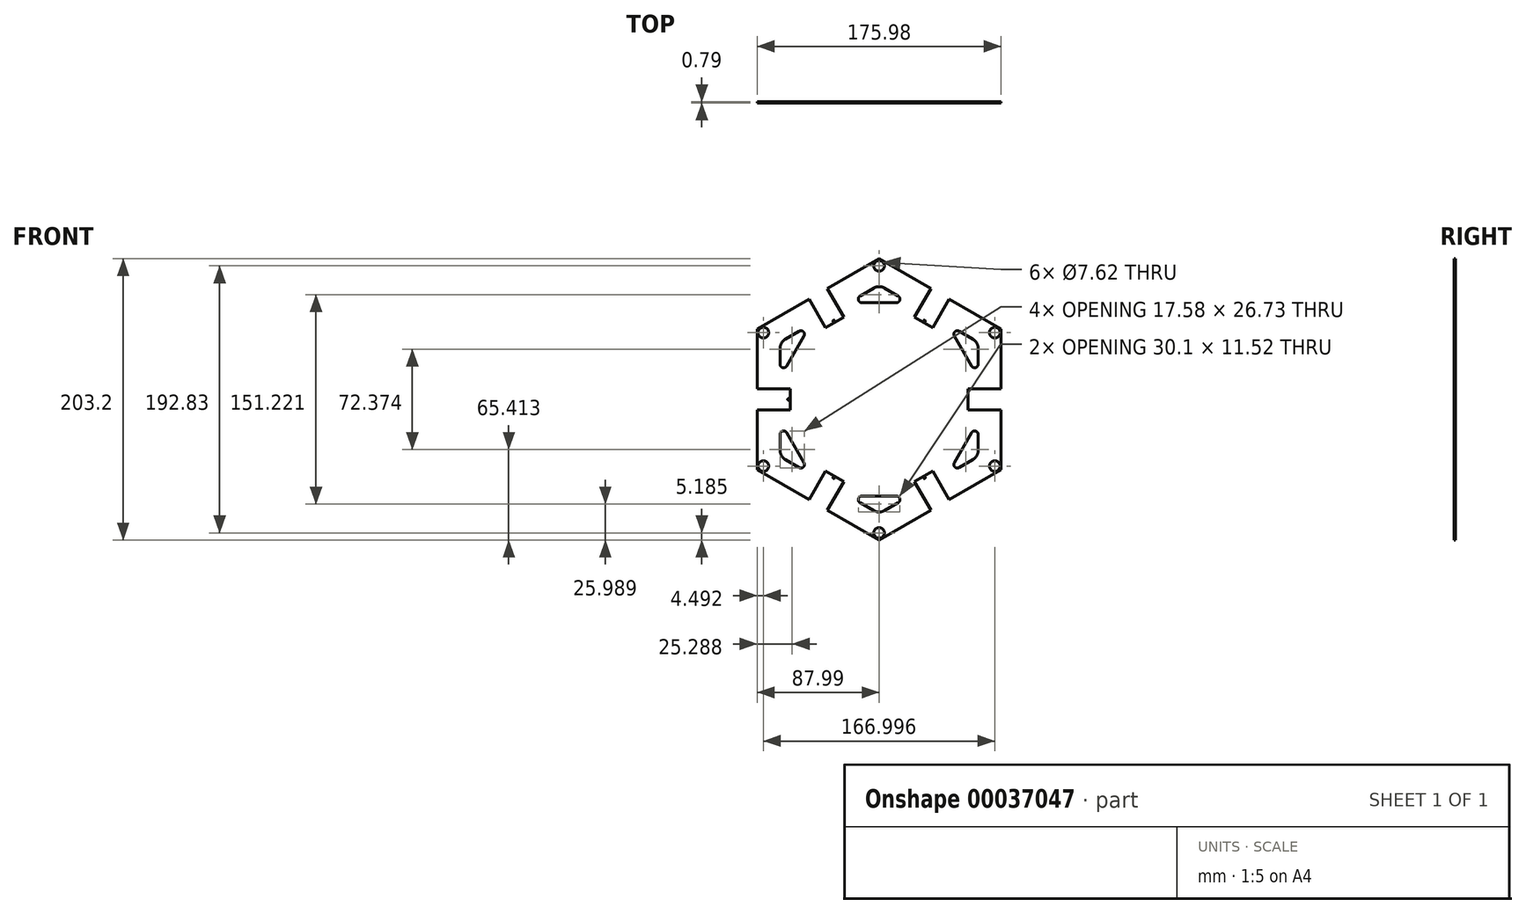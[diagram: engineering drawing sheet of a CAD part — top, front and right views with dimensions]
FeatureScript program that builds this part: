
annotation { "Feature Type Name" : "Feature", "Feature Type Description" : "" }
export const myFeature = defineFeature(function(context is Context, id is Id, definition is map)
    precondition{}
    {
        {
            var Q0;
            Q0=qCreatedBy(makeId("Front.planeOp"),FACE);
            var sketch = newSketch(context, id + "F0", { "sketchPlane" : qUnion([Q0])});
            skCircle(sketch, "E0.cCircle", {"center": v(0, 0) * mm, "radius": 87.99 * mm, "construction": true});
            skLineSegment(sketch, "E0.0", {"start": v(0, 101.6) * mm, "end": v(87.99, 50.8) * mm});
            skLineSegment(sketch, "E0.1", {"start": v(87.99, 50.8) * mm, "end": v(87.99, -50.8) * mm});
            skLineSegment(sketch, "E0.2", {"start": v(87.99, -50.8) * mm, "end": v(0, -101.6) * mm});
            skLineSegment(sketch, "E0.3", {"start": v(0, -101.6) * mm, "end": v(-87.99, -50.8) * mm});
            skLineSegment(sketch, "E0.4", {"start": v(-87.99, -50.8) * mm, "end": v(-87.99, 50.8) * mm});
            skLineSegment(sketch, "E0.5", {"start": v(-87.99, 50.8) * mm, "end": v(0, 101.6) * mm});
            skPoint(sketch, "E0.0.midPoint", {"position": v(44, 76.2) * mm});
            skSolve(sketch);
        }
        {
            var Q0;
            Q0=qSketchRegion(id+"F0",true);
            extrude(context, id + "F1", {"entities" : qUnion([Q0]), "depth" : 0.8 * mm});
        }
        {
            var Q0;
            Q0=makeQuery(id+"F1.opExtrude","CAP_FACE",FACE,{"disambiguationData":[OSD([sQuery(id+"F0.wireOp",EDGE,"E0.0"),sQuery(id+"F0.wireOp",EDGE,"E0.1"),sQuery(id+"F0.wireOp",EDGE,"E0.2"),sQuery(id+"F0.wireOp",EDGE,"E0.3"),sQuery(id+"F0.wireOp",EDGE,"E0.4"),sQuery(id+"F0.wireOp",EDGE,"E0.5")])],"isStart":false});
            var sketch = newSketch(context, id + "F2", { "sketchPlane" : qUnion([Q0])});
            skSolve(sketch);
        }
        {
            var Q0;
            Q0=qCreatedBy(makeId("Front.planeOp"),FACE);
            var sketch = newSketch(context, id + "F3", { "sketchPlane" : qUnion([Q0])});
            skLineSegment(sketch, "E1.bottom", {"start": v(87.99, 10.16) * mm, "end": v(102.7, 10.16) * mm});
            skLineSegment(sketch, "E1.top", {"start": v(87.99, -10.16) * mm, "end": v(102.7, -10.16) * mm});
            skLineSegment(sketch, "E1.left", {"start": v(87.99, 10.16) * mm, "end": v(87.99, -10.16) * mm});
            skLineSegment(sketch, "E1.right", {"start": v(102.7, 10.16) * mm, "end": v(102.7, -10.16) * mm});
            skPoint(sketch, "E2", {"position": v(87.99, 0) * mm});
            skLineSegment(sketch, "E3.1.0", {"start": v(52.8, -71.12) * mm, "end": v(60.15, -83.86) * mm});
            skLineSegment(sketch, "E3.1.1", {"start": v(52.8, -71.12) * mm, "end": v(35.2, -81.28) * mm});
            skLineSegment(sketch, "E3.1.2", {"start": v(60.15, -83.86) * mm, "end": v(42.55, -94.02) * mm});
            skLineSegment(sketch, "E3.1.3", {"start": v(35.2, -81.28) * mm, "end": v(42.55, -94.02) * mm});
            skLineSegment(sketch, "E3.2.0", {"start": v(-35.2, -81.28) * mm, "end": v(-42.55, -94.02) * mm});
            skLineSegment(sketch, "E3.2.1", {"start": v(-35.2, -81.28) * mm, "end": v(-52.8, -71.12) * mm});
            skLineSegment(sketch, "E3.2.2", {"start": v(-42.55, -94.02) * mm, "end": v(-60.15, -83.86) * mm});
            skLineSegment(sketch, "E3.2.3", {"start": v(-52.8, -71.12) * mm, "end": v(-60.15, -83.86) * mm});
            skLineSegment(sketch, "E3.3.0", {"start": v(-87.99, -10.16) * mm, "end": v(-102.7, -10.16) * mm});
            skLineSegment(sketch, "E3.3.1", {"start": v(-87.99, -10.16) * mm, "end": v(-87.99, 10.16) * mm});
            skLineSegment(sketch, "E3.3.2", {"start": v(-102.7, -10.16) * mm, "end": v(-102.7, 10.16) * mm});
            skLineSegment(sketch, "E3.3.3", {"start": v(-87.99, 10.16) * mm, "end": v(-102.7, 10.16) * mm});
            skLineSegment(sketch, "E3.4.0", {"start": v(-52.8, 71.12) * mm, "end": v(-60.15, 83.86) * mm});
            skLineSegment(sketch, "E3.4.1", {"start": v(-52.8, 71.12) * mm, "end": v(-35.2, 81.28) * mm});
            skLineSegment(sketch, "E3.4.2", {"start": v(-60.15, 83.86) * mm, "end": v(-42.55, 94.02) * mm});
            skLineSegment(sketch, "E3.4.3", {"start": v(-35.2, 81.28) * mm, "end": v(-42.55, 94.02) * mm});
            skLineSegment(sketch, "E3.5.0", {"start": v(35.2, 81.28) * mm, "end": v(42.55, 94.02) * mm});
            skLineSegment(sketch, "E3.5.1", {"start": v(35.2, 81.28) * mm, "end": v(52.8, 71.12) * mm});
            skLineSegment(sketch, "E3.5.2", {"start": v(42.55, 94.02) * mm, "end": v(60.15, 83.86) * mm});
            skLineSegment(sketch, "E3.5.3", {"start": v(52.8, 71.12) * mm, "end": v(60.15, 83.86) * mm});
            skPoint(sketch, "E3.center", {"position": v(0, 0) * mm});
            skLineSegment(sketch, "E3.anchor1", {"start": v(0, 0) * mm, "end": v(87.99, 10.16) * mm, "construction": true});
            skLineSegment(sketch, "E3.anchor2", {"start": v(0, 0) * mm, "end": v(35.2, 81.28) * mm, "construction": true});
            skPoint(sketch, "E4.1.0", {"position": v(48.34, 83.72) * mm});
            skPoint(sketch, "E4.2.0", {"position": v(-48.34, 83.72) * mm});
            skPoint(sketch, "E4.3.0", {"position": v(-96.67, 0) * mm});
            skPoint(sketch, "E4.4.0", {"position": v(-48.34, -83.72) * mm});
            skPoint(sketch, "E4.5.0", {"position": v(48.34, -83.72) * mm});
            skSolve(sketch);
        }
        {
            var Q0;
            Q0=makeQuery(id+"F2.imprint","IMPRINT",FACE,{"disambiguationData":[TD([[makeQuery(id+"F2.imprint","IMPRINT",EDGE,{"derivedFrom":makeQuery(id+"F1.opExtrude","CAP_EDGE",EDGE,{"disambiguationData":[OSD([sQuery(id+"F0.wireOp",EDGE,"E0.0")])],"isStart":false})}),-1.0]])]});
            var sketch = newSketch(context, id + "F4", { "sketchPlane" : qUnion([Q0])});
            skPoint(sketch, "E5.0", {"position": v(93.15, 0) * mm});
            skLineSegment(sketch, "E6.bottom", {"start": v(64, 7.62) * mm, "end": v(94.49, 7.62) * mm});
            skLineSegment(sketch, "E6.top", {"start": v(64, -7.62) * mm, "end": v(94.49, -7.62) * mm});
            skLineSegment(sketch, "E6.left", {"start": v(64, 7.62) * mm, "end": v(64, -7.62) * mm});
            skLineSegment(sketch, "E6.right", {"start": v(94.49, 7.62) * mm, "end": v(94.49, -7.62) * mm});
            skPoint(sketch, "E7", {"position": v(64, 0) * mm});
            skLineSegment(sketch, "E8", {"start": v(64, 0) * mm, "end": v(65.35, 0) * mm, "construction": true});
            skLineSegment(sketch, "E9", {"start": v(93.15, 0) * mm, "end": v(94.49, 0) * mm, "construction": true});
            skPoint(sketch, "E10.1.0", {"position": v(32.67, 56.6) * mm});
            skPoint(sketch, "E10.1.1", {"position": v(32, 55.43) * mm});
            skLineSegment(sketch, "E10.1.2", {"start": v(38.6, 51.62) * mm, "end": v(53.84, 78.02) * mm});
            skLineSegment(sketch, "E10.1.3", {"start": v(25.4, 59.24) * mm, "end": v(40.64, 85.64) * mm});
            skPoint(sketch, "E10.1.4", {"position": v(46.57, 80.67) * mm});
            skLineSegment(sketch, "E10.1.5", {"start": v(40.64, 85.64) * mm, "end": v(53.84, 78.02) * mm});
            skLineSegment(sketch, "E10.1.6", {"start": v(32, 55.43) * mm, "end": v(32.67, 56.6) * mm, "construction": true});
            skLineSegment(sketch, "E10.1.7", {"start": v(25.4, 59.24) * mm, "end": v(38.6, 51.62) * mm});
            skCircle(sketch, "E10.1.8", {"center": v(46.57, 80.67) * mm, "radius": 0.64 * mm});
            skCircle(sketch, "E10.1.9", {"center": v(32.67, 56.6) * mm, "radius": 0.64 * mm});
            skLineSegment(sketch, "E10.1.10", {"start": v(46.57, 80.67) * mm, "end": v(47.24, 81.83) * mm, "construction": true});
            skPoint(sketch, "E10.2.0", {"position": v(-32.67, 56.6) * mm});
            skPoint(sketch, "E10.2.1", {"position": v(-32, 55.43) * mm});
            skLineSegment(sketch, "E10.2.2", {"start": v(-25.4, 59.24) * mm, "end": v(-40.64, 85.64) * mm});
            skLineSegment(sketch, "E10.2.3", {"start": v(-38.6, 51.62) * mm, "end": v(-53.84, 78.02) * mm});
            skPoint(sketch, "E10.2.4", {"position": v(-46.57, 80.67) * mm});
            skLineSegment(sketch, "E10.2.5", {"start": v(-53.84, 78.02) * mm, "end": v(-40.64, 85.64) * mm});
            skLineSegment(sketch, "E10.2.6", {"start": v(-32, 55.43) * mm, "end": v(-32.67, 56.6) * mm, "construction": true});
            skLineSegment(sketch, "E10.2.7", {"start": v(-38.6, 51.62) * mm, "end": v(-25.4, 59.24) * mm});
            skCircle(sketch, "E10.2.8", {"center": v(-46.57, 80.67) * mm, "radius": 0.64 * mm});
            skCircle(sketch, "E10.2.9", {"center": v(-32.67, 56.6) * mm, "radius": 0.64 * mm});
            skLineSegment(sketch, "E10.2.10", {"start": v(-46.57, 80.67) * mm, "end": v(-47.24, 81.83) * mm, "construction": true});
            skPoint(sketch, "E10.3.0", {"position": v(-65.35, 0) * mm});
            skPoint(sketch, "E10.3.1", {"position": v(-64, 0) * mm});
            skLineSegment(sketch, "E10.3.2", {"start": v(-64, 7.62) * mm, "end": v(-94.49, 7.62) * mm});
            skLineSegment(sketch, "E10.3.3", {"start": v(-64, -7.62) * mm, "end": v(-94.49, -7.62) * mm});
            skPoint(sketch, "E10.3.4", {"position": v(-93.15, 0) * mm});
            skLineSegment(sketch, "E10.3.5", {"start": v(-94.49, -7.62) * mm, "end": v(-94.49, 7.62) * mm});
            skLineSegment(sketch, "E10.3.6", {"start": v(-64, 0) * mm, "end": v(-65.35, 0) * mm, "construction": true});
            skLineSegment(sketch, "E10.3.7", {"start": v(-64, -7.62) * mm, "end": v(-64, 7.62) * mm});
            skCircle(sketch, "E10.3.8", {"center": v(-93.15, 0) * mm, "radius": 0.64 * mm});
            skCircle(sketch, "E10.3.9", {"center": v(-65.35, 0) * mm, "radius": 0.64 * mm});
            skLineSegment(sketch, "E10.3.10", {"start": v(-93.15, 0) * mm, "end": v(-94.49, 0) * mm, "construction": true});
            skPoint(sketch, "E10.4.0", {"position": v(-32.67, -56.6) * mm});
            skPoint(sketch, "E10.4.1", {"position": v(-32, -55.43) * mm});
            skLineSegment(sketch, "E10.4.2", {"start": v(-38.6, -51.62) * mm, "end": v(-53.84, -78.02) * mm});
            skLineSegment(sketch, "E10.4.3", {"start": v(-25.4, -59.24) * mm, "end": v(-40.64, -85.64) * mm});
            skPoint(sketch, "E10.4.4", {"position": v(-46.57, -80.67) * mm});
            skLineSegment(sketch, "E10.4.5", {"start": v(-40.64, -85.64) * mm, "end": v(-53.84, -78.02) * mm});
            skLineSegment(sketch, "E10.4.6", {"start": v(-32, -55.43) * mm, "end": v(-32.67, -56.6) * mm, "construction": true});
            skLineSegment(sketch, "E10.4.7", {"start": v(-25.4, -59.24) * mm, "end": v(-38.6, -51.62) * mm});
            skCircle(sketch, "E10.4.8", {"center": v(-46.57, -80.67) * mm, "radius": 0.64 * mm});
            skCircle(sketch, "E10.4.9", {"center": v(-32.67, -56.6) * mm, "radius": 0.64 * mm});
            skLineSegment(sketch, "E10.4.10", {"start": v(-46.57, -80.67) * mm, "end": v(-47.24, -81.83) * mm, "construction": true});
            skPoint(sketch, "E10.5.0", {"position": v(32.67, -56.6) * mm});
            skPoint(sketch, "E10.5.1", {"position": v(32, -55.43) * mm});
            skLineSegment(sketch, "E10.5.2", {"start": v(25.4, -59.24) * mm, "end": v(40.64, -85.64) * mm});
            skLineSegment(sketch, "E10.5.3", {"start": v(38.6, -51.62) * mm, "end": v(53.84, -78.02) * mm});
            skPoint(sketch, "E10.5.4", {"position": v(46.57, -80.67) * mm});
            skLineSegment(sketch, "E10.5.5", {"start": v(53.84, -78.02) * mm, "end": v(40.64, -85.64) * mm});
            skLineSegment(sketch, "E10.5.6", {"start": v(32, -55.43) * mm, "end": v(32.67, -56.6) * mm, "construction": true});
            skLineSegment(sketch, "E10.5.7", {"start": v(38.6, -51.62) * mm, "end": v(25.4, -59.24) * mm});
            skCircle(sketch, "E10.5.8", {"center": v(46.57, -80.67) * mm, "radius": 0.64 * mm});
            skCircle(sketch, "E10.5.9", {"center": v(32.67, -56.6) * mm, "radius": 0.64 * mm});
            skLineSegment(sketch, "E10.5.10", {"start": v(46.57, -80.67) * mm, "end": v(47.24, -81.83) * mm, "construction": true});
            skPoint(sketch, "E10.center", {"position": v(0, 0) * mm});
            skSolve(sketch);
        }
        {
            var Q0;
            Q0=qSketchRegion(id+"F4",true);
            extrude(context, id + "F5", {"entities" : qUnion([Q0]), "operationType" : NewBodyOperationType.REMOVE, "endBound" : BoundingType.THROUGH_ALL, "oppositeDirection" : true, "depth" : 25.4 * mm});
        }
        {
            var Q0;
            Q0=makeQuery(id+"F2.imprint","IMPRINT",FACE,{"disambiguationData":[TD([[makeQuery(id+"F2.imprint","IMPRINT",EDGE,{"derivedFrom":makeQuery(id+"F1.opExtrude","CAP_EDGE",EDGE,{"disambiguationData":[OSD([sQuery(id+"F0.wireOp",EDGE,"E0.0")])],"isStart":false})}),-1.0]])]});
            var sketch = newSketch(context, id + "F6", { "sketchPlane" : qUnion([Q0])});
            skLineSegment(sketch, "E11", {"start": v(91.28, 52.7) * mm, "end": v(75.72, 43.72) * mm, "construction": true});
            skLineSegment(sketch, "E12", {"start": v(75.72, 43.72) * mm, "end": v(79, 55.98) * mm, "construction": true});
            skLineSegment(sketch, "E13", {"start": v(79, 55.98) * mm, "end": v(91.28, 52.7) * mm, "construction": true});
            skLineSegment(sketch, "E14", {"start": v(91.28, 52.7) * mm, "end": v(87.99, 40.43) * mm, "construction": true});
            skLineSegment(sketch, "E15", {"start": v(87.99, 40.43) * mm, "end": v(75.72, 43.72) * mm, "construction": true});
            skPoint(sketch, "E16", {"position": v(83.5, 48.2) * mm});
            skPoint(sketch, "E17.1.0", {"position": v(0, 96.42) * mm});
            skPoint(sketch, "E17.2.0", {"position": v(-83.5, 48.2) * mm});
            skPoint(sketch, "E17.3.0", {"position": v(-83.5, -48.2) * mm});
            skPoint(sketch, "E17.4.0", {"position": v(0, -96.42) * mm});
            skPoint(sketch, "E17.5.0", {"position": v(83.5, -48.2) * mm});
            skPoint(sketch, "E17.center", {"position": v(0, 0) * mm});
            skSolve(sketch);
        }
        {
            var Q0;
            Q0=sQuery(id+"F6.wireOp",VERTEX,"E17.5.0");
            var Q1;
            Q1=sQuery(id+"F6.wireOp",VERTEX,"E17.4.0");
            var Q2;
            Q2=sQuery(id+"F6.wireOp",VERTEX,"E17.3.0");
            var Q3;
            Q3=sQuery(id+"F6.wireOp",VERTEX,"E17.2.0");
            var Q4;
            Q4=sQuery(id+"F6.wireOp",VERTEX,"E17.1.0");
            var Q5;
            Q5=sQuery(id+"F6.wireOp",VERTEX,"E16");
            var Q6;
            Q6=makeQuery(id+"F1.opExtrude","SWEPT_BODY",BODY,{"disambiguationData":[OSD([sQuery(id+"F0.wireOp",EDGE,"E0.0"),sQuery(id+"F0.wireOp",EDGE,"E0.1"),sQuery(id+"F0.wireOp",EDGE,"E0.2"),sQuery(id+"F0.wireOp",EDGE,"E0.3"),sQuery(id+"F0.wireOp",EDGE,"E0.4"),sQuery(id+"F0.wireOp",EDGE,"E0.5")])]});
            hole(context, id + "F7", {"style" : HoleStyle.SIMPLE, "holeDiameter" : 7.62 * mm, "endStyle" : HoleEndStyle.THROUGH, "locations" : qUnion([Q0, Q1, Q2, Q3, Q4, Q5]), "scope" : qUnion([Q6])});
        }
        {
            var Q0;
            Q0=makeQuery(id+"F2.imprint","IMPRINT",FACE,{"disambiguationData":[TD([[makeQuery(id+"F2.imprint","IMPRINT",EDGE,{"derivedFrom":makeQuery(id+"F1.opExtrude","CAP_EDGE",EDGE,{"disambiguationData":[OSD([sQuery(id+"F0.wireOp",EDGE,"E0.0")])],"isStart":false})}),-1.0]])]});
            var sketch = newSketch(context, id + "F8", { "sketchPlane" : qUnion([Q0])});
            skLineSegment(sketch, "E18.rect.bottom", {"start": v(28.58, 44.45) * mm, "end": v(-28.57, 44.45) * mm});
            skLineSegment(sketch, "E18.rect.top", {"start": v(28.58, -44.45) * mm, "end": v(-28.57, -44.45) * mm});
            skLineSegment(sketch, "E18.rect.left", {"start": v(28.58, 44.45) * mm, "end": v(28.58, -44.45) * mm});
            skLineSegment(sketch, "E18.rect.right", {"start": v(-28.57, 44.45) * mm, "end": v(-28.57, -44.45) * mm});
            skPoint(sketch, "E18.rect.middle", {"position": v(0, 0) * mm});
            skSolve(sketch);
        }
        {
            var Q0;
            {var subQ26=sQuery(id+"F4.wireOp",EDGE,"E6.left");Q0=makeQuery(id+"F4.imprint","IMPRINT",FACE,{"disambiguationData":[TD([[makeQuery(id+"F4.imprint","IMPRINT",EDGE,{"derivedFrom":subQ26}),-1.0]])]});}
            var sketch = newSketch(context, id + "F9", { "sketchPlane" : qUnion([Q0])});
            skLineSegment(sketch, "E19", {"start": v(-12.52, 69.85) * mm, "end": v(12.52, 69.85) * mm});
            skLineSegment(sketch, "E20", {"start": v(13.79, 74.59) * mm, "end": v(3.81, 80.35) * mm});
            skLineSegment(sketch, "E21", {"start": v(-3.8, 80.35) * mm, "end": v(-13.79, 74.59) * mm});
            skLineSegment(sketch, "E22", {"start": v(0, 0) * mm, "end": v(0, 101.6) * mm, "construction": true});
            skPoint(sketch, "E23.visualSharp", {"position": v(-22, 69.85) * mm});
            skArc(sketch, "E23.filletArc", {"start": v(-13.79, 74.59) * mm, "mid": v(-14.97, 71.73) * mm, "end": v(-12.52, 69.85) * mm});
            skPoint(sketch, "E24.visualSharp", {"position": v(22, 69.85) * mm});
            skArc(sketch, "E24.filletArc", {"start": v(12.52, 69.85) * mm, "mid": v(14.97, 71.73) * mm, "end": v(13.79, 74.59) * mm});
            skPoint(sketch, "E25", {"position": v(0, 69.85) * mm});
            skPoint(sketch, "E26.visualSharp", {"position": v(0, 82.55) * mm});
            skArc(sketch, "E26.filletArc", {"start": v(3.81, 80.35) * mm, "mid": v(0, 81.37) * mm, "end": v(-3.8, 80.35) * mm});
            skPoint(sketch, "E27.1.0", {"position": v(-49.5, 53.97) * mm});
            skPoint(sketch, "E27.1.1", {"position": v(-71.5, 41.28) * mm});
            skLineSegment(sketch, "E27.1.2", {"start": v(-57.7, 49.24) * mm, "end": v(-67.68, 43.47) * mm});
            skLineSegment(sketch, "E27.1.3", {"start": v(-66.75, 24.08) * mm, "end": v(-54.23, 45.77) * mm});
            skLineSegment(sketch, "E27.1.4", {"start": v(-71.5, 36.88) * mm, "end": v(-71.5, 25.35) * mm});
            skArc(sketch, "E27.1.5", {"start": v(-54.23, 45.77) * mm, "mid": v(-54.64, 48.83) * mm, "end": v(-57.7, 49.24) * mm});
            skArc(sketch, "E27.1.6", {"start": v(-71.5, 25.35) * mm, "mid": v(-69.6, 22.9) * mm, "end": v(-66.75, 24.08) * mm});
            skPoint(sketch, "E27.1.7", {"position": v(-60.5, 34.93) * mm});
            skArc(sketch, "E27.1.8", {"start": v(-67.68, 43.47) * mm, "mid": v(-70.47, 40.69) * mm, "end": v(-71.5, 36.88) * mm});
            skPoint(sketch, "E27.2.0", {"position": v(-71.5, -15.88) * mm});
            skPoint(sketch, "E27.2.1", {"position": v(-71.5, -41.27) * mm});
            skLineSegment(sketch, "E27.2.2", {"start": v(-71.5, -25.35) * mm, "end": v(-71.5, -36.88) * mm});
            skLineSegment(sketch, "E27.2.3", {"start": v(-54.23, -45.77) * mm, "end": v(-66.75, -24.08) * mm});
            skLineSegment(sketch, "E27.2.4", {"start": v(-67.68, -43.47) * mm, "end": v(-57.7, -49.24) * mm});
            skArc(sketch, "E27.2.5", {"start": v(-66.75, -24.08) * mm, "mid": v(-69.6, -22.9) * mm, "end": v(-71.5, -25.35) * mm});
            skArc(sketch, "E27.2.6", {"start": v(-57.7, -49.24) * mm, "mid": v(-54.64, -48.83) * mm, "end": v(-54.23, -45.77) * mm});
            skPoint(sketch, "E27.2.7", {"position": v(-60.5, -34.92) * mm});
            skArc(sketch, "E27.2.8", {"start": v(-71.5, -36.88) * mm, "mid": v(-70.47, -40.69) * mm, "end": v(-67.68, -43.47) * mm});
            skPoint(sketch, "E27.3.0", {"position": v(-22, -69.85) * mm});
            skPoint(sketch, "E27.3.1", {"position": v(0, -82.55) * mm});
            skLineSegment(sketch, "E27.3.2", {"start": v(-13.79, -74.59) * mm, "end": v(-3.81, -80.35) * mm});
            skLineSegment(sketch, "E27.3.3", {"start": v(12.52, -69.85) * mm, "end": v(-12.52, -69.85) * mm});
            skLineSegment(sketch, "E27.3.4", {"start": v(3.8, -80.35) * mm, "end": v(13.79, -74.59) * mm});
            skArc(sketch, "E27.3.5", {"start": v(-12.52, -69.85) * mm, "mid": v(-14.97, -71.73) * mm, "end": v(-13.79, -74.59) * mm});
            skArc(sketch, "E27.3.6", {"start": v(13.79, -74.59) * mm, "mid": v(14.97, -71.73) * mm, "end": v(12.52, -69.85) * mm});
            skPoint(sketch, "E27.3.7", {"position": v(0, -69.85) * mm});
            skArc(sketch, "E27.3.8", {"start": v(-3.81, -80.35) * mm, "mid": v(0, -81.37) * mm, "end": v(3.8, -80.35) * mm});
            skPoint(sketch, "E27.4.0", {"position": v(49.5, -53.97) * mm});
            skPoint(sketch, "E27.4.1", {"position": v(71.5, -41.28) * mm});
            skLineSegment(sketch, "E27.4.2", {"start": v(57.7, -49.24) * mm, "end": v(67.68, -43.47) * mm});
            skLineSegment(sketch, "E27.4.3", {"start": v(66.75, -24.08) * mm, "end": v(54.23, -45.77) * mm});
            skLineSegment(sketch, "E27.4.4", {"start": v(71.5, -36.88) * mm, "end": v(71.5, -25.35) * mm});
            skArc(sketch, "E27.4.5", {"start": v(54.23, -45.77) * mm, "mid": v(54.64, -48.83) * mm, "end": v(57.7, -49.24) * mm});
            skArc(sketch, "E27.4.6", {"start": v(71.5, -25.35) * mm, "mid": v(69.6, -22.9) * mm, "end": v(66.75, -24.08) * mm});
            skPoint(sketch, "E27.4.7", {"position": v(60.5, -34.93) * mm});
            skArc(sketch, "E27.4.8", {"start": v(67.68, -43.47) * mm, "mid": v(70.47, -40.69) * mm, "end": v(71.5, -36.88) * mm});
            skPoint(sketch, "E27.5.0", {"position": v(71.5, 15.88) * mm});
            skPoint(sketch, "E27.5.1", {"position": v(71.5, 41.28) * mm});
            skLineSegment(sketch, "E27.5.2", {"start": v(71.5, 25.35) * mm, "end": v(71.5, 36.88) * mm});
            skLineSegment(sketch, "E27.5.3", {"start": v(54.23, 45.77) * mm, "end": v(66.75, 24.08) * mm});
            skLineSegment(sketch, "E27.5.4", {"start": v(67.68, 43.47) * mm, "end": v(57.7, 49.24) * mm});
            skArc(sketch, "E27.5.5", {"start": v(66.75, 24.08) * mm, "mid": v(69.6, 22.9) * mm, "end": v(71.5, 25.35) * mm});
            skArc(sketch, "E27.5.6", {"start": v(57.7, 49.24) * mm, "mid": v(54.64, 48.83) * mm, "end": v(54.23, 45.77) * mm});
            skPoint(sketch, "E27.5.7", {"position": v(60.5, 34.93) * mm});
            skArc(sketch, "E27.5.8", {"start": v(71.5, 36.88) * mm, "mid": v(70.47, 40.69) * mm, "end": v(67.68, 43.47) * mm});
            skPoint(sketch, "E27.center", {"position": v(0, 0) * mm});
            skSolve(sketch);
        }
        {
            var Q0;
            Q0=qSketchRegion(id+"F9",true);
            extrude(context, id + "F10", {"entities" : qUnion([Q0]), "operationType" : NewBodyOperationType.REMOVE, "endBound" : BoundingType.THROUGH_ALL, "oppositeDirection" : true, "depth" : 25.4 * mm});
        }
    });
